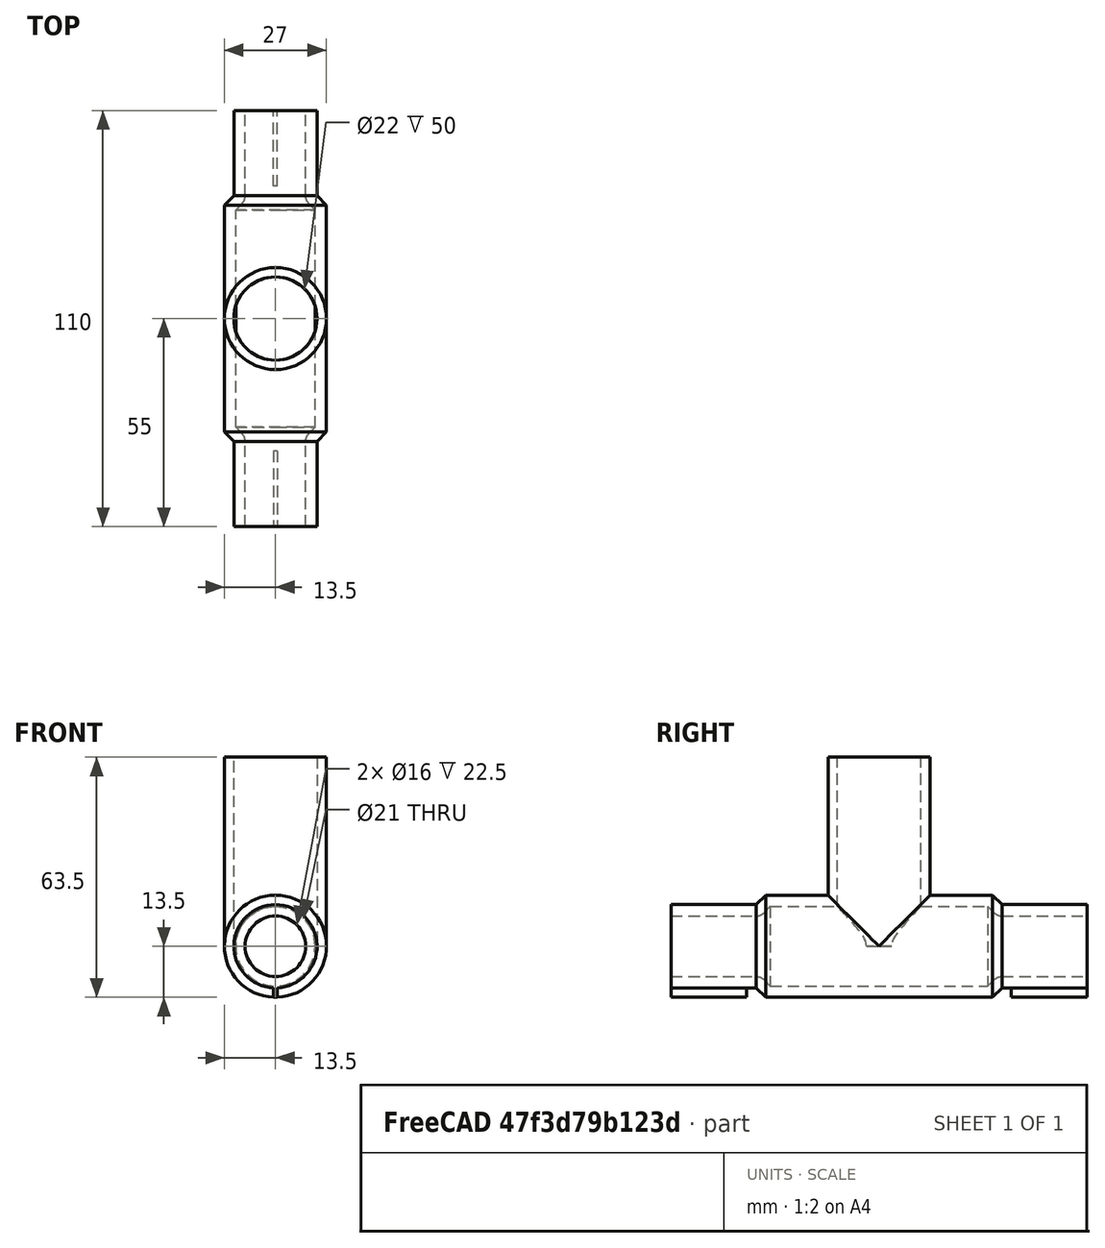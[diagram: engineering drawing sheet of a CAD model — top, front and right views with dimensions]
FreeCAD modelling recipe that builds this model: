
FCSTD DOCUMENT  (FreeCAD 0.19R20802 (Git))
Label: NIV_CPAP_T_Piece
License: All rights reserved
LicenseURL: http://en.wikipedia.org/wiki/All_rights_reserved
objects: TechDraw::DrawViewDimension×11, TechDraw::DrawViewBalloon×6, Sketcher::SketchObject×4, TechDraw::DrawProjGroupItem×3, PartDesign::Plane×2, PartDesign::Pad×2, TechDraw::DrawViewAnnotation×2, PartDesign::Revolution×1, PartDesign::Thickness×1, PartDesign::Pocket×1, PartDesign::Mirrored×1, PartDesign::Body×1, TechDraw::DrawSVGTemplate×1, TechDraw::DrawProjGroup×1, TechDraw::DrawPage×1
note: 18 computed .brp shape members not serialized (recipe doc carries the construction recipe); baked Part::Feature solids carry a one-line shape summary decoded from their .brp

FEATURE [Sketcher::SketchObject] Sketch
  MapMode = 5
  Placement = pos=(0,0,0) rot=(0.57735,0.57735,0.57735;2.0944rad)
  Support = -> [YZ_Plane]
  sketch-geometry (9):
    g0: LineSegment StartX=-55 StartY=0 StartZ=0 EndX=-55 EndY=11 EndZ=0
    g1: LineSegment StartX=-55 StartY=11 StartZ=0 EndX=-32.5 EndY=11 EndZ=0
    g2: LineSegment StartX=-32.5 StartY=11 StartZ=0 EndX=-30 EndY=13.5 EndZ=0
    g3: LineSegment StartX=-30 StartY=13.5 StartZ=0 EndX=30 EndY=13.5 EndZ=0
    g4: LineSegment StartX=30 StartY=13.5 StartZ=0 EndX=32.5 EndY=11 EndZ=0
    g5: LineSegment StartX=32.5 StartY=11 StartZ=0 EndX=55 EndY=11 EndZ=0
    g6: LineSegment StartX=55 StartY=11 StartZ=0 EndX=55 EndY=0 EndZ=0
    g7: LineSegment StartX=55 StartY=0 StartZ=0 EndX=-55 EndY=0 EndZ=0
    g8: LineSegment [constr] StartX=0 StartY=13.5 StartZ=0 EndX=0 EndY=0 EndZ=0
  constraints (25):
    c: PointOnObject(g0,g-1)
    c: Vertical(g0)
    c: Coincident(g1,g0)
    c: Horizontal(g1)
    c: Coincident(g2,g1)
    c: Coincident(g3,g2)
    c: Horizontal(g3)
    c: Coincident(g4,g3)
    c: Coincident(g5,g4)
    c: Horizontal(g5)
    c: Coincident(g6,g5)
    c: PointOnObject(g6,g-1)
    c: Vertical(g6)
    c: Coincident(g7,g6)
    c: Coincident(g7,g0)
    c: DistanceY(g0,g0) = 11
    c: DistanceX(g3,g3) = 60
    c: Coincident(g8,g-1)
    c: PointOnObject(g8,g3)
    c: Symmetric(g2,g3,g8)
    c: Symmetric(g1,g4,g8)
    c: Equal(g1,g5)
    c: DistanceX(g7,g7) = 110
    c: Angle(g2,g1) = 2.35619
    c: DistanceY(g5,g3) = 2.5
FEATURE [PartDesign::Revolution] Revolution
  AllowMultiFace = false
  Angle = 360
  Axis = (1e-16,1,-1e-16)
  Base = (0,0,0)
  Placement = pos=(0,0,0) rot=(0.57735,0.57735,0.57735;2.0944rad)
  Profile = -> Sketch
  ReferenceAxis = -> Y_Axis
FEATURE [PartDesign::Thickness] Thickness
  Base = -> Revolution [Face7,Face1]
  BaseFeature = -> Revolution
  Intersection = false
  Join = 0
  Mode = 0
  Reversed = true
  SupportTransform = false
  Value = 3
FEATURE [PartDesign::Plane] DatumPlane
  Length = 60
  MapMode = 2
  Placement = pos=(0,0,50) rot=(0,0,1;0rad)
  ResizeMode = 0
  Width = 124.832
FEATURE [Sketcher::SketchObject] Sketch001
  MapMode = 5
  Placement = pos=(0,0,50) rot=(0,0,1;0rad)
  Support = -> [DatumPlane]
  sketch-geometry (1):
    g0: Circle CenterX=0 CenterY=0 CenterZ=0 NormalX=0 NormalY=0 NormalZ=1 AngleXU=0 Radius=13.5
  constraints (2):
    c: Coincident(g0,g-1)
    c: Radius(g0) = 13.5
FEATURE [PartDesign::Pad] Pad
  AllowMultiFace = false
  BaseFeature = -> Thickness
  Length = 10
  Length2 = 100
  Profile = -> Sketch001
  Type = 3
  UpToFace = -> Thickness [Face3]
FEATURE [Sketcher::SketchObject] Sketch002
  MapMode = 5
  Placement = pos=(0,0,50) rot=(0,0,1;0rad)
  Support = -> [DatumPlane]
  sketch-geometry (1):
    g0: Circle CenterX=0 CenterY=0 CenterZ=0 NormalX=0 NormalY=0 NormalZ=1 AngleXU=0 Radius=11
  constraints (2):
    c: Coincident(g0,g-1)
    c: Radius(g0) = 11
FEATURE [PartDesign::Pocket] Pocket
  AllowMultiFace = false
  BaseFeature = -> Pad
  Length = 50
  Length2 = 100
  Profile = -> Sketch002
  Type = 0
FEATURE [PartDesign::Plane] DatumPlane001
  Length = 60
  MapMode = 2
  Placement = pos=(0,0,-13.5) rot=(0,0,1;0rad)
  ResizeMode = 0
  Width = 124.832
FEATURE [Sketcher::SketchObject] Sketch003
  ExternalGeometry = -> [Pocket]
  MapMode = 5
  Placement = pos=(0,0,-13.5) rot=(0,0,1;0rad)
  Support = -> [DatumPlane001]
  sketch-geometry (4):
    g0: LineSegment StartX=-0.5 StartY=55 StartZ=0 EndX=0.5 EndY=55 EndZ=0
    g1: LineSegment StartX=0.5 StartY=55 StartZ=0 EndX=0.5 EndY=35 EndZ=0
    g2: LineSegment StartX=0.5 StartY=35 StartZ=0 EndX=-0.5 EndY=35 EndZ=0
    g3: LineSegment StartX=-0.5 StartY=35 StartZ=0 EndX=-0.5 EndY=55 EndZ=0
  constraints (12):
    c: Coincident(g0,g1)
    c: Coincident(g1,g2)
    c: Coincident(g2,g3)
    c: Coincident(g3,g0)
    c: Horizontal(g0)
    c: Horizontal(g2)
    c: Vertical(g1)
    c: Vertical(g3)
    c: DistanceX(g0,g0) = 1
    c: Distance(g0,g-2) = 0.5
    c: PointOnObject(g0,g-3)
    c: DistanceY(g1,g1) = 20
FEATURE [PartDesign::Pad] Pad001
  AllowMultiFace = false
  BaseFeature = -> Pocket
  Length = 10
  Length2 = 100
  Profile = -> Sketch003
  Type = 3
  UpToFace = -> Pocket [Face11]
FEATURE [PartDesign::Mirrored] Mirrored
  BaseFeature = -> Pad001
  MirrorPlane = -> XZ_Plane
  Originals = -> [Pad001]
FEATURE [PartDesign::Body] Body
  Group = -> [Sketch,Revolution,Thickness,DatumPlane,Sketch001,Pad,Sketch002,Pocket,DatumPlane001,Sketch003,Pad001,Mirrored]
  Origin = -> Origin
  Tip = -> Mirrored
FEATURE [TechDraw::DrawSVGTemplate] Template
  Height = 297
  Orientation = 0
  Width = 210
FEATURE [TechDraw::DrawProjGroupItem] ProjItem  label="Front"
  CoarseView = false
  Direction = (1,0,0)
  Focus = 100
  HardHidden = true
  IsoCount = 0
  IsoHidden = false
  IsoVisible = false
  LockPosition = true
  Perspective = false
  Rotation = 0
  RotationVector = (0,1,0)
  ScaleType = 2
  SeamHidden = false
  SeamVisible = false
  SmoothHidden = false
  SmoothVisible = true
  Source = -> [Mirrored]
  Type = 0
  X = 0
  XDirection = (0,1,0)
  Y = 0
FEATURE [TechDraw::DrawProjGroupItem] ProjItem003  label="Top"
  CoarseView = false
  Direction = (0,0,1)
  Focus = 100
  HardHidden = true
  IsoCount = 0
  IsoHidden = false
  IsoVisible = false
  LockPosition = false
  Perspective = false
  Rotation = 0
  RotationVector = (1,0,0)
  ScaleType = 2
  SeamHidden = false
  SeamVisible = false
  SmoothHidden = false
  SmoothVisible = true
  Source = -> [Mirrored]
  Type = 4
  X = 0
  XDirection = (0,1,0)
  Y = -99.6503
FEATURE [TechDraw::DrawProjGroupItem] ProjItem004  label="FrontBottomLeft"
  CoarseView = false
  Direction = (0.57735,-0.57735,-0.57735)
  Focus = 100
  HardHidden = false
  IsoCount = 0
  IsoHidden = false
  IsoVisible = false
  LockPosition = false
  Perspective = false
  Rotation = 0
  RotationVector = (1,0,0)
  ScaleType = 2
  SeamHidden = false
  SeamVisible = false
  SmoothHidden = false
  SmoothVisible = true
  Source = -> [Mirrored]
  Type = 8
  X = 57.6272
  XDirection = (0.707107,0.707107,0)
  Y = 98.8775
FEATURE [TechDraw::DrawProjGroup] ProjGroup
  Anchor = -> ProjItem
  AutoDistribute = false
  LockPosition = false
  ProjectionType = 0
  Rotation = 0
  ScaleType = 0
  Source = -> [Mirrored]
  Views = -> [ProjItem,ProjItem003,ProjItem004]
  X = 100.025
  Y = 151.432
  spacingX = 15
  spacingY = 15
FEATURE [TechDraw::DrawViewDimension] Dimension
  Arbitrary = false
  FormatSpec = %.2f
  Inverted = false
  LockPosition = false
  MeasureType = 1
  OverTolerance = 0
  References2D = -> [ProjItem]
  Rotation = 0
  ScaleType = 0
  TheoreticalExact = false
  Type = 1
  UnderTolerance = 0
  X = 0.410783
  Y = -52.71
FEATURE [TechDraw::DrawViewDimension] Dimension001
  Arbitrary = false
  FormatSpec = %.2f
  Inverted = false
  LockPosition = false
  MeasureType = 1
  OverTolerance = 0
  References2D = -> [ProjItem]
  Rotation = 0
  ScaleType = 0
  TheoreticalExact = false
  Type = 1
  UnderTolerance = 0
  X = -42.6369
  Y = 10.2944
FEATURE [TechDraw::DrawViewDimension] Dimension002
  Arbitrary = false
  FormatSpec = %.2f
  Inverted = false
  LockPosition = false
  MeasureType = 1
  OverTolerance = 0
  References2D = -> [ProjItem]
  Rotation = 0
  ScaleType = 0
  TheoreticalExact = false
  Type = 1
  UnderTolerance = 0
  X = 0
  Y = -39.8287
FEATURE [TechDraw::DrawViewDimension] Dimension003
  Arbitrary = false
  FormatSpec = %.2f
  Inverted = false
  LockPosition = false
  MeasureType = 1
  OverTolerance = 0
  References2D = -> [ProjItem]
  Rotation = 0
  ScaleType = 0
  TheoreticalExact = false
  Type = 1
  UnderTolerance = 0
  X = 46.0027
  Y = -41.4417
FEATURE [TechDraw::DrawViewDimension] Dimension004
  Arbitrary = false
  FormatSpec = %.2f
  Inverted = false
  LockPosition = false
  MeasureType = 1
  OverTolerance = 0
  References2D = -> [ProjItem]
  Rotation = 0
  ScaleType = 0
  TheoreticalExact = false
  Type = 2
  UnderTolerance = 0
  X = 61.4863
  Y = -23.5624
FEATURE [TechDraw::DrawViewDimension] Dimension005
  Arbitrary = false
  FormatSpec = Ø%.2f
  Inverted = false
  LockPosition = false
  MeasureType = 1
  OverTolerance = 0
  References2D = -> [ProjItem]
  Rotation = 0
  ScaleType = 0
  TheoreticalExact = false
  Type = 1
  UnderTolerance = 0
  X = -0.600443
  Y = 52.7655
FEATURE [TechDraw::DrawViewDimension] Dimension006
  Arbitrary = false
  FormatSpec = Ø%.2f
  Inverted = false
  LockPosition = false
  MeasureType = 1
  OverTolerance = 0
  References2D = -> [ProjItem]
  Rotation = 0
  ScaleType = 0
  TheoreticalExact = false
  Type = 1
  UnderTolerance = 0
  X = 0
  Y = 42.387
FEATURE [TechDraw::DrawViewDimension] Dimension008
  Arbitrary = false
  FormatSpec = Ø%.2f
  Inverted = false
  LockPosition = false
  MeasureType = 1
  OverTolerance = 0
  References2D = -> [ProjItem003]
  Rotation = 0
  ScaleType = 0
  TheoreticalExact = false
  Type = 2
  UnderTolerance = 0
  X = -64.457
  Y = -0.150111
FEATURE [TechDraw::DrawViewDimension] Dimension009
  Arbitrary = false
  FormatSpec = Ø%.2f
  Inverted = false
  LockPosition = false
  MeasureType = 1
  OverTolerance = 0
  References2D = -> [ProjItem003]
  Rotation = 0
  ScaleType = 0
  TheoreticalExact = false
  Type = 2
  UnderTolerance = 0
  X = -76.4659
  Y = 0.750554
FEATURE [TechDraw::DrawViewDimension] Dimension010
  Arbitrary = false
  FormatSpec = %.2f
  Inverted = false
  LockPosition = false
  MeasureType = 1
  OverTolerance = 0
  References2D = -> [ProjItem003]
  Rotation = 0
  ScaleType = 0
  TheoreticalExact = false
  Type = 2
  UnderTolerance = 0
  X = 59.0615
  Y = 5.66981
FEATURE [TechDraw::DrawViewDimension] Dimension011
  Arbitrary = false
  FormatSpec = %.2f
  Inverted = false
  LockPosition = false
  MeasureType = 1
  OverTolerance = 0
  References2D = -> [ProjItem]
  Rotation = 0
  ScaleType = 0
  TheoreticalExact = false
  Type = 2
  UnderTolerance = 0
  X = 31.6837
  Y = 16.2551
FEATURE [TechDraw::DrawViewAnnotation] Annotation
  Caption = Scale 1:1
  Font = osifont
  LineSpace = 80
  LockPosition = false
  MaxWidth = -1
  Rotation = 0
  ScaleType = 0
  Text = NIV_CPAP_T_piece
  TextSize = 5
  TextStyle = 0
  X = 25.7416
  Y = 284.743
FEATURE [TechDraw::DrawViewBalloon] Balloon
  EndType = 0
  KinkLength = 5
  LockPosition = false
  OriginX = 49.4766
  OriginY = -32.6543
  Rotation = 0
  ScaleType = 0
  Shape = 0
  ShapeScale = 1
  SourceView = -> ProjItem
  Text = 1
  TextWrapLen = -1
  X = 79.4379
  Y = -56.9252
FEATURE [TechDraw::DrawViewBalloon] Balloon001
  EndType = 0
  KinkLength = 5
  LockPosition = false
  OriginX = 47.4007
  OriginY = 0.467893
  Rotation = 0
  ScaleType = 0
  Shape = 0
  ShapeScale = 1
  SourceView = -> ProjItem003
  Text = 1
  TextWrapLen = -1
  X = 80.2849
  Y = 21.4207
FEATURE [TechDraw::DrawViewAnnotation] Annotation001
  Font = osifont
  LineSpace = 80
  LockPosition = false
  MaxWidth = -1
  Rotation = 0
  ScaleType = 0
  Text = 1. Print support feature, to be removed after print
  TextSize = 5
  TextStyle = 0
  X = 151.74
  Y = 4.34421
FEATURE [TechDraw::DrawViewBalloon] Balloon002
  EndType = 0
  KinkLength = 5
  LockPosition = false
  OriginX = -45.629
  OriginY = -32.408
  Rotation = 0
  ScaleType = 0
  Shape = 0
  ShapeScale = 1
  SourceView = -> ProjItem
  Text = 1
  TextWrapLen = -1
  X = -71.3023
  Y = -53.0386
FEATURE [TechDraw::DrawViewBalloon] Balloon003
  EndType = 0
  KinkLength = 5
  LockPosition = false
  OriginX = -44.645
  OriginY = 0.494396
  Rotation = 0
  ScaleType = 0
  Shape = 0
  ShapeScale = 1
  SourceView = -> ProjItem003
  Text = 1
  TextWrapLen = -1
  X = -71.0156
  Y = 29.3917
FEATURE [TechDraw::DrawViewBalloon] Balloon004
  EndType = 0
  KinkLength = 5
  LockPosition = false
  OriginX = -33.0398
  OriginY = -0.399289
  Rotation = 0
  ScaleType = 0
  Shape = 0
  ShapeScale = 1
  SourceView = -> ProjItem004
  Text = 1
  TextWrapLen = -1
  X = -51.1675
  Y = -11.6468
FEATURE [TechDraw::DrawViewBalloon] Balloon005
  EndType = 0
  KinkLength = 5
  LockPosition = false
  OriginX = 31.4619
  OriginY = -37.6669
  Rotation = 0
  ScaleType = 0
  Shape = 0
  ShapeScale = 1
  SourceView = -> ProjItem004
  Text = 1
  TextWrapLen = -1
  X = 14.4809
  Y = -47.481
FEATURE [TechDraw::DrawPage] Page
  KeepUpdated = true
  NextBalloonIndex = 8
  ProjectionType = 0
  Template = -> Template
  Views = -> [ProjGroup,Dimension,Dimension001,Dimension002,Dimension003,Dimension004,Dimension005,Dimension006,Dimension008,Dimension009,Dimension010,Dimension011,Annotation,Balloon,Balloon001,Annotation001,Balloon002,Balloon003,Balloon004,Balloon005]
